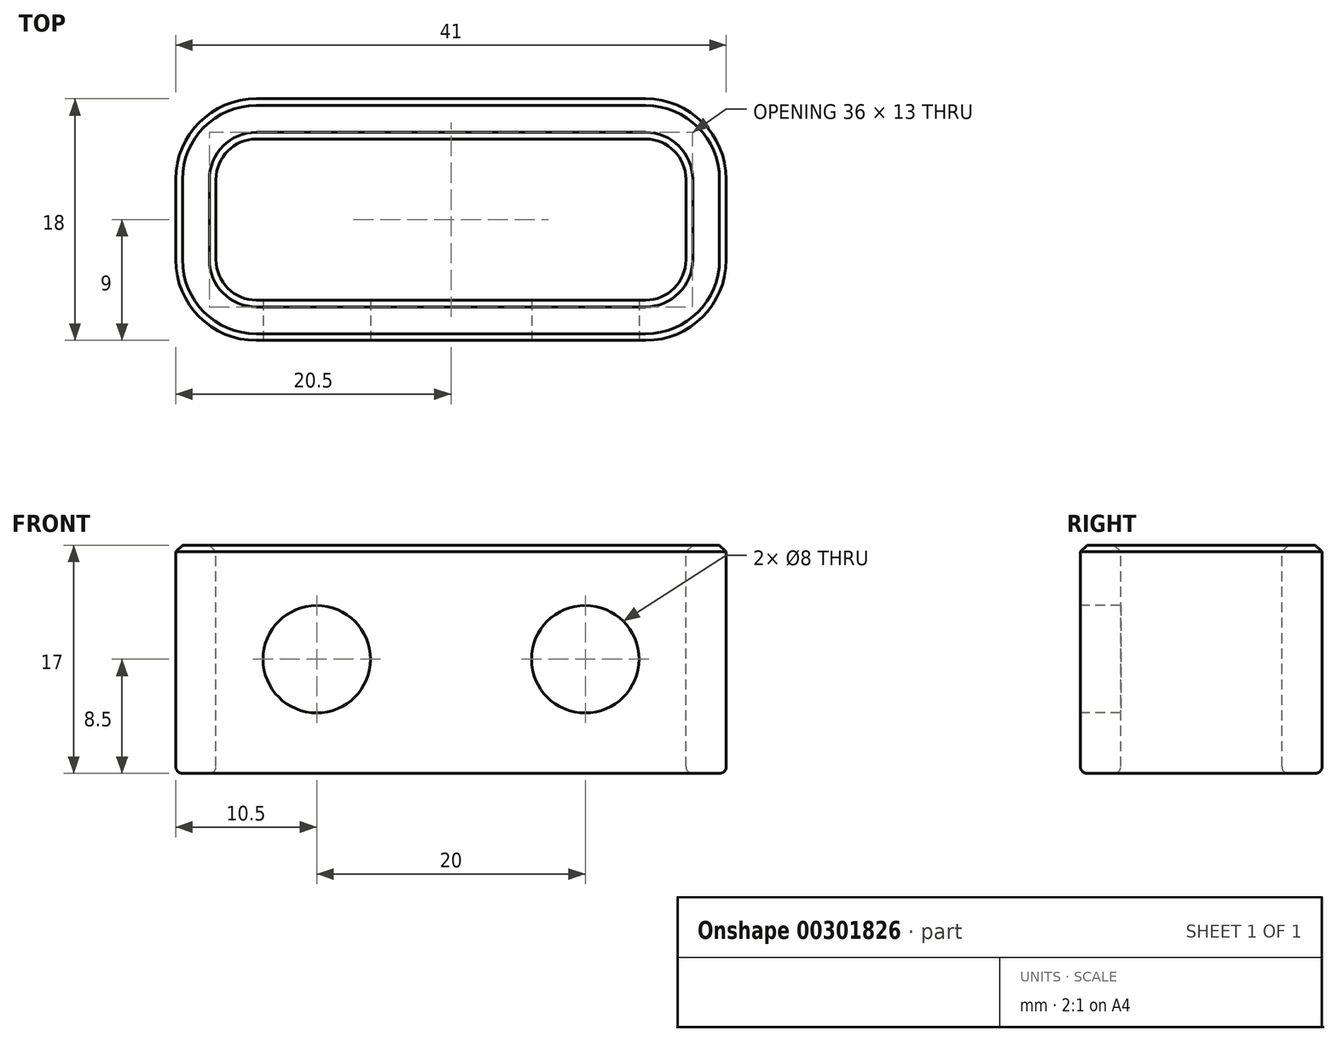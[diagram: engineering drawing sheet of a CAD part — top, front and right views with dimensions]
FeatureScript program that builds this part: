
annotation { "Feature Type Name" : "Feature", "Feature Type Description" : "" }
export const myFeature = defineFeature(function(context is Context, id is Id, definition is map)
    precondition{}
    {
        {
            var Q0;
            Q0=qCreatedBy(makeId("Top.planeOp"),FACE);
            var sketch = newSketch(context, id + "F0", { "sketchPlane" : qUnion([Q0])});
            skLineSegment(sketch, "E0.bottom", {"start": v(-14.5, -9) * mm, "end": v(14.5, -9) * mm});
            skLineSegment(sketch, "E0.top", {"start": v(-14.5, 9) * mm, "end": v(14.5, 9) * mm});
            skLineSegment(sketch, "E0.left", {"start": v(-20.5, -3) * mm, "end": v(-20.5, 3) * mm});
            skLineSegment(sketch, "E0.right", {"start": v(20.5, -3) * mm, "end": v(20.5, 3) * mm});
            skPoint(sketch, "E0.middle", {"position": v(0, 0) * mm});
            skPoint(sketch, "E1.visualSharp", {"position": v(-20.5, 9) * mm});
            skArc(sketch, "E1.filletArc", {"start": v(-14.5, 9) * mm, "mid": v(-18.74, 7.24) * mm, "end": v(-20.5, 3) * mm});
            skPoint(sketch, "E2.visualSharp", {"position": v(20.5, 9) * mm});
            skArc(sketch, "E2.filletArc", {"start": v(20.5, 3) * mm, "mid": v(18.74, 7.24) * mm, "end": v(14.5, 9) * mm});
            skPoint(sketch, "E3.visualSharp", {"position": v(20.5, -9) * mm});
            skArc(sketch, "E3.filletArc", {"start": v(14.5, -9) * mm, "mid": v(18.74, -7.24) * mm, "end": v(20.5, -3) * mm});
            skPoint(sketch, "E4.visualSharp", {"position": v(-20.5, -9) * mm});
            skArc(sketch, "E4.filletArc", {"start": v(-20.5, -3) * mm, "mid": v(-18.74, -7.24) * mm, "end": v(-14.5, -9) * mm});
            skSolve(sketch);
        }
        {
            var Q0;
            Q0=qSketchRegion(id+"F0",true);
            extrude(context, id + "F1", {"entities" : qUnion([Q0]), "depth" : 17 * mm});
        }
        {
            var Q0;
            Q0=makeQuery(id+"F1.opExtrude","CAP_FACE",FACE,{"disambiguationData":[OSD([sQuery(id+"F0.wireOp",EDGE,"E0.bottom"),sQuery(id+"F0.wireOp",EDGE,"E0.top"),sQuery(id+"F0.wireOp",EDGE,"E0.left"),sQuery(id+"F0.wireOp",EDGE,"E0.right"),sQuery(id+"F0.wireOp",EDGE,"E1.filletArc"),sQuery(id+"F0.wireOp",EDGE,"E2.filletArc"),sQuery(id+"F0.wireOp",EDGE,"E3.filletArc"),sQuery(id+"F0.wireOp",EDGE,"E4.filletArc")])],"isStart":false});
            var Q1;
            Q1=makeQuery(id+"F1.opExtrude","CAP_FACE",FACE,{"disambiguationData":[OSD([sQuery(id+"F0.wireOp",EDGE,"E0.bottom"),sQuery(id+"F0.wireOp",EDGE,"E0.top"),sQuery(id+"F0.wireOp",EDGE,"E0.left"),sQuery(id+"F0.wireOp",EDGE,"E0.right"),sQuery(id+"F0.wireOp",EDGE,"E1.filletArc"),sQuery(id+"F0.wireOp",EDGE,"E2.filletArc"),sQuery(id+"F0.wireOp",EDGE,"E3.filletArc"),sQuery(id+"F0.wireOp",EDGE,"E4.filletArc")])],"isStart":true});
            shell(context, id + "F2", {"entities" : qUnion([Q0, Q1]), "thickness" : 3 * mm});
        }
        {
            var Q0;
            Q0=makeQuery(id+"F1.opExtrude","SWEPT_FACE",FACE,{"disambiguationData":[OSD([sQuery(id+"F0.wireOp",EDGE,"E0.bottom")])]});
            var sketch = newSketch(context, id + "F3", { "sketchPlane" : qUnion([Q0])});
            skCircle(sketch, "E5", {"center": v(-10, 8.5) * mm, "radius": 4 * mm});
            skCircle(sketch, "E6", {"center": v(10, 8.5) * mm, "radius": 4 * mm});
            skSolve(sketch);
        }
        {
            var Q0;
            Q0=qSketchRegion(id+"F3",true);
            extrude(context, id + "F4", {"entities" : qUnion([Q0]), "operationType" : NewBodyOperationType.REMOVE, "oppositeDirection" : true, "depth" : 5 * mm});
        }
        {
            var Q0;
            Q0=makeQuery(id+"F1.opExtrude","CAP_EDGE",EDGE,{"disambiguationData":[OSD([sQuery(id+"F0.wireOp",EDGE,"E0.top")])],"isStart":true});
            var Q1;
            {var subQ0=sQuery(id+"F0.wireOp",EDGE,"E0.bottom");Q1=makeQuery(id+"F2.opShell","OFFSET_EDGE",EDGE,{"disambiguationData":[OSD([subQ0]),TDD([makeQuery(id+"F1.opExtrude","CAP_EDGE",EDGE,{"disambiguationData":[OSD([subQ0])],"isStart":true})])]});}
            var Q2;
            Q2=makeQuery(id+"F4.boolean.opBoolean","COPY",EDGE,{"derivedFrom":makeQuery(id+"F4.opExtrude","CAP_EDGE",EDGE,{"disambiguationData":[OSD([sQuery(id+"F3.wireOp",EDGE,"E6")])],"isStart":true})});
            var Q3;
            Q3=makeQuery(id+"F4.boolean.opBoolean","COPY",EDGE,{"derivedFrom":makeQuery(id+"F4.opExtrude","CAP_EDGE",EDGE,{"disambiguationData":[OSD([sQuery(id+"F3.wireOp",EDGE,"E5")])],"isStart":true})});
            fillet(context, id + "F5", {"entities" : qUnion([Q0, Q1, Q2, Q3]), "radius" : 0.5 * mm, "tangentPropagation" : true, "allowEdgeOverflow" : false});
        }
        {
            var Q0;
            Q0=makeQuery(id+"F1.opExtrude","CAP_EDGE",EDGE,{"disambiguationData":[OSD([sQuery(id+"F0.wireOp",EDGE,"E0.bottom")])],"isStart":false});
            var Q1;
            {var subQ0=sQuery(id+"F0.wireOp",EDGE,"E0.bottom");Q1=makeQuery(id+"F2.opShell","OFFSET_EDGE",EDGE,{"disambiguationData":[OSD([subQ0]),TDD([makeQuery(id+"F1.opExtrude","CAP_EDGE",EDGE,{"disambiguationData":[OSD([subQ0])],"isStart":false})])]});}
            chamfer(context, id + "F6", {"entities" : qUnion([Q0, Q1]), "width" : 0.5 * mm, "tangentPropagation" : true});
        }
    });
